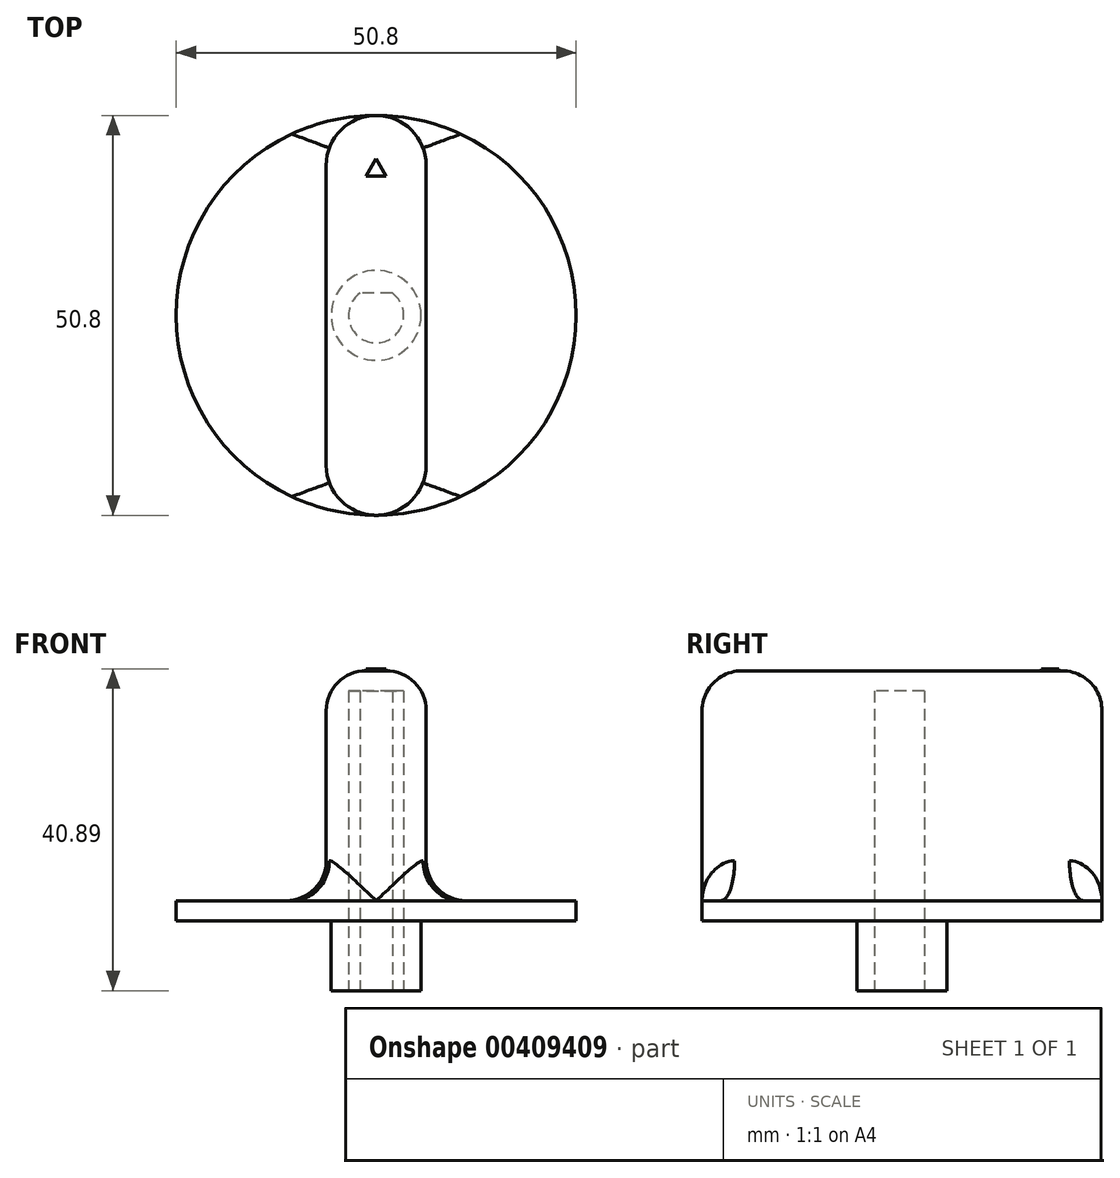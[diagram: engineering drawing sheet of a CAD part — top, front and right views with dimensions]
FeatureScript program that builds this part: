
annotation { "Feature Type Name" : "Feature", "Feature Type Description" : "" }
export const myFeature = defineFeature(function(context is Context, id is Id, definition is map)
    precondition{}
    {
        {
            var Q0;
            Q0=qCreatedBy(makeId("Top.planeOp"),FACE);
            var sketch = newSketch(context, id + "F0", { "sketchPlane" : qUnion([Q0])});
            skArc(sketch, "E0", {"start": v(-2.05, 2.84) * mm, "mid": v(0, -3.5) * mm, "end": v(2.05, 2.84) * mm});
            skCircle(sketch, "E1", {"center": v(0, 0) * mm, "radius": 5.72 * mm});
            skCircle(sketch, "E2", {"center": v(0, 0) * mm, "radius": 25.4 * mm});
            skLineSegment(sketch, "E3", {"start": v(6.35, 0) * mm, "end": v(6.35, 19.05) * mm});
            skArc(sketch, "E4", {"start": v(6.35, 19.05) * mm, "mid": v(0, 25.4) * mm, "end": v(-6.35, 19.05) * mm});
            skLineSegment(sketch, "E5", {"start": v(-6.35, 0) * mm, "end": v(-6.35, 19.05) * mm});
            skArc(sketch, "E6.MirrorC", {"start": v(6.35, -19.05) * mm, "mid": v(0, -25.4) * mm, "end": v(-6.35, -19.05) * mm});
            skLineSegment(sketch, "E7.MirrorCS", {"start": v(6.35, 0) * mm, "end": v(6.35, -19.05) * mm});
            skLineSegment(sketch, "E8.MirrorCS", {"start": v(-6.35, 0) * mm, "end": v(-6.35, -19.05) * mm});
            skLineSegment(sketch, "E9", {"start": v(0, 2.84) * mm, "end": v(2.05, 2.84) * mm});
            skLineSegment(sketch, "E10", {"start": v(0, 2.84) * mm, "end": v(-2.05, 2.84) * mm});
            skPoint(sketch, "E11.start.orphan", {"position": v(0, -3.5) * mm});
            skSolve(sketch);
        }
        {
            var Q0;
            Q0=makeQuery(id+"F0.imprint","IMPRINT",FACE,{"disambiguationData":[TD([[makeQuery(id+"F0.imprint","IMPRINT",EDGE,{"derivedFrom":sQuery(id+"F0.wireOp",EDGE,"E0")}),-1.0]])]});
            extrude(context, id + "F1", {"entities" : qUnion([Q0]), "depth" : 31.75 * mm});
        }
        {
            var Q0;
            Q0=makeQuery(id+"F1.opExtrude","CAP_FACE",FACE,{"disambiguationData":[OSD([sQuery(id+"F0.wireOp",EDGE,"E0"),sQuery(id+"F0.wireOp",EDGE,"E1"),sQuery(id+"F0.wireOp",EDGE,"E9"),sQuery(id+"F0.wireOp",EDGE,"E10")])],"isStart":true});
            extrude(context, id + "F2", {"entities" : qUnion([Q0]), "operationType" : NewBodyOperationType.ADD, "depth" : 8.9 * mm});
        }
        {
            var Q0;
            Q0=makeQuery(id+"F0.imprint","IMPRINT",FACE,{"disambiguationData":[TD([[makeQuery(id+"F0.imprint","IMPRINT",EDGE,{"derivedFrom":sQuery(id+"F0.wireOp",EDGE,"E1")}),-1.0]])]});
            extrude(context, id + "F3", {"entities" : qUnion([Q0]), "operationType" : NewBodyOperationType.ADD, "depth" : 31.75 * mm});
        }
        {
            var Q0;
            Q0 = qSketchRegion(id + "F0", true);
            extrude(context, id + "F4", {"entities" : qUnion([Q0]), "operationType" : NewBodyOperationType.ADD, "depth" : 2.54 * mm});
        }
        {
            var Q0;
            {var subQ0=sQuery(id+"F0.wireOp",EDGE,"E1");Q0=makeQuery(id+"F3.boolean.opBoolean","MERGE",FACE,{"derivedFrom":[makeQuery(id+"F1.opExtrude","CAP_FACE",FACE,{"disambiguationData":[OSD([sQuery(id+"F0.wireOp",EDGE,"E0"),subQ0,sQuery(id+"F0.wireOp",EDGE,"E9"),sQuery(id+"F0.wireOp",EDGE,"E10")])],"isStart":false}),makeQuery(id+"F3.opExtrude","CAP_FACE",FACE,{"disambiguationData":[OSD([subQ0,sQuery(id+"F0.wireOp",EDGE,"E3"),sQuery(id+"F0.wireOp",EDGE,"E4"),sQuery(id+"F0.wireOp",EDGE,"E5"),sQuery(id+"F0.wireOp",EDGE,"E6.MirrorC"),sQuery(id+"F0.wireOp",EDGE,"E7.MirrorCS"),sQuery(id+"F0.wireOp",EDGE,"E8.MirrorCS")])],"isStart":false})]});}
            var sketch = newSketch(context, id + "F5", { "sketchPlane" : qUnion([Q0])});
            skLineSegment(sketch, "E12.0", {"start": v(6.35, 0) * mm, "end": v(6.35, 19.05) * mm});
            skArc(sketch, "E12.1", {"start": v(6.35, 19.05) * mm, "mid": v(0, 25.4) * mm, "end": v(-6.35, 19.05) * mm});
            skLineSegment(sketch, "E12.2", {"start": v(-6.35, 0) * mm, "end": v(-6.35, 19.05) * mm});
            skLineSegment(sketch, "E12.3", {"start": v(-6.35, 0) * mm, "end": v(-6.35, -19.05) * mm});
            skArc(sketch, "E12.4", {"start": v(6.35, -19.05) * mm, "mid": v(0, -25.4) * mm, "end": v(-6.35, -19.05) * mm});
            skLineSegment(sketch, "E12.5", {"start": v(6.35, 0) * mm, "end": v(6.35, -19.05) * mm});
            skSolve(sketch);
        }
        {
            var Q0;
            Q0 = qSketchRegion(id + "F5", true);
            extrude(context, id + "F6", {"entities" : qUnion([Q0]), "operationType" : NewBodyOperationType.ADD, "oppositeDirection" : true, "depth" : 2.54 * mm});
        }
        {
            var Q0;
            Q0=makeQuery(id+"F4.boolean.opBoolean","INTERSECT",EDGE,{"derivedFrom":[makeQuery(id+"F3.opExtrude","SWEPT_FACE",FACE,{"disambiguationData":[OSD([sQuery(id+"F0.wireOp",EDGE,"E5"),sQuery(id+"F0.wireOp",EDGE,"E8.MirrorCS")])]}),makeQuery(id+"F4.opExtrude","CAP_FACE",FACE,{"disambiguationData":[OSD([sQuery(id+"F0.wireOp",EDGE,"E1"),sQuery(id+"F0.wireOp",EDGE,"E2")])],"isStart":false})]});
            var Q1;
            Q1=makeQuery(id+"F3.opExtrude","CAP_EDGE",EDGE,{"disambiguationData":[OSD([sQuery(id+"F0.wireOp",EDGE,"E5"),sQuery(id+"F0.wireOp",EDGE,"E8.MirrorCS")])],"isStart":false});
            fillet(context, id + "F7", {"entities" : qUnion([Q0, Q1]), "radius" : 5.08 * mm, "tangentPropagation" : true, "allowEdgeOverflow" : false});
        }
        {
            var Q0;
            {var subQ0=sQuery(id+"F0.wireOp",EDGE,"E1");Q0=makeQuery(id+"F6.boolean.opBoolean","MERGE",FACE,{"derivedFrom":[makeQuery(id+"F3.boolean.opBoolean","MERGE",FACE,{"derivedFrom":[makeQuery(id+"F1.opExtrude","CAP_FACE",FACE,{"disambiguationData":[OSD([sQuery(id+"F0.wireOp",EDGE,"E0"),subQ0,sQuery(id+"F0.wireOp",EDGE,"E9"),sQuery(id+"F0.wireOp",EDGE,"E10")])],"isStart":false}),makeQuery(id+"F3.opExtrude","CAP_FACE",FACE,{"disambiguationData":[OSD([subQ0,sQuery(id+"F0.wireOp",EDGE,"E3"),sQuery(id+"F0.wireOp",EDGE,"E4"),sQuery(id+"F0.wireOp",EDGE,"E5"),sQuery(id+"F0.wireOp",EDGE,"E6.MirrorC"),sQuery(id+"F0.wireOp",EDGE,"E7.MirrorCS"),sQuery(id+"F0.wireOp",EDGE,"E8.MirrorCS")])],"isStart":false})]}),makeQuery(id+"F6.opExtrude","CAP_FACE",FACE,{"disambiguationData":[OSD([sQuery(id+"F5.wireOp",EDGE,"E12.0"),sQuery(id+"F5.wireOp",EDGE,"E12.1"),sQuery(id+"F5.wireOp",EDGE,"E12.2"),sQuery(id+"F5.wireOp",EDGE,"E12.3"),sQuery(id+"F5.wireOp",EDGE,"E12.4"),sQuery(id+"F5.wireOp",EDGE,"E12.5")])],"isStart":true})]});}
            var sketch = newSketch(context, id + "F8", { "sketchPlane" : qUnion([Q0])});
            skCircle(sketch, "E13.cCircle", {"center": v(0, 18.44) * mm, "radius": 1.47 * mm, "construction": true});
            skLineSegment(sketch, "E13.0", {"start": v(1.27, 17.7) * mm, "end": v(-1.27, 17.7) * mm});
            skLineSegment(sketch, "E13.1", {"start": v(-1.27, 17.7) * mm, "end": v(0, 19.9) * mm});
            skLineSegment(sketch, "E13.2", {"start": v(0, 19.9) * mm, "end": v(1.27, 17.7) * mm});
            skSolve(sketch);
        }
        {
            var Q0;
            Q0=makeQuery(id+"F8.imprint","IMPRINT",FACE,{"disambiguationData":[TD([[makeQuery(id+"F8.imprint","IMPRINT",EDGE,{"derivedFrom":sQuery(id+"F8.wireOp",EDGE,"E13.0")}),-1.0]])]});
            extrude(context, id + "F9", {"entities" : qUnion([Q0]), "operationType" : NewBodyOperationType.ADD, "depth" : 0.25 * mm});
        }
    });
